# Revit family: Zumtobel MIRL M600L L12+L15
name_source: partatom
category: Lighting Fixtures
revit_build: Autodesk Revit 2018 (Build: 20170223_1515(x64)
units: mm (PartAtom-declared; Revit-internal decimal feet)

## family parameters
Cut with Voids When Loaded = No
Host = Face
Light Source = Yes
OmniClass Number = 23.80.70.11
OmniClass Title = Luminaries for Internal Lighting
Part Type = Normal
Room Calculation Point = No
Round Connector Dimension = Use Diameter
Shared = No

## types (2) — shared parameters
Apparent Load = 31 VA
Assembly Code = D5020200
Color Filter = 16777215
Description = Recessed LED luminaire
Dimming Lamp Color Temperature Shift = <None>
Emit Shape Visible in Rendering = No
Emit from Rectangle Length = 150 mm
Height = 70 mm  [stored 0.229659 ft]
Lamp = LED
Manufacturer = Zumtobel Lighting
Tilt Angle = 90.00°
Voltage = 230 V
Width = 150 mm
zero-valued in all types: Default Elevation

## per-type parameters (varying)
| type | Emit from Rectangle Width | Length | Model | Photometric Web File | URL |
| MIRL M600L 12x150 | 1198 mm  [stored 3.93045 ft] | 1198 mm  [stored 3.93045 ft] | 42185476 | 42185476_(STD_LEO).IES | www.zumtobel.de/42185476 |
| MIRL M600L 15x114 | 1498 mm  [stored 4.9147 ft] | 1498 mm  [stored 4.9147 ft] | 42185475 | 42185475_(STD_LEO).IES | www.zumtobel.de/42185475 |

note: [stored X ft] marks values corroborated as IEEE doubles in the binary element streams (Revit-internal decimal feet)

## geometry (parser evidence)
native form markers: Sweep x3
no freeform markers — native parametric forms only
